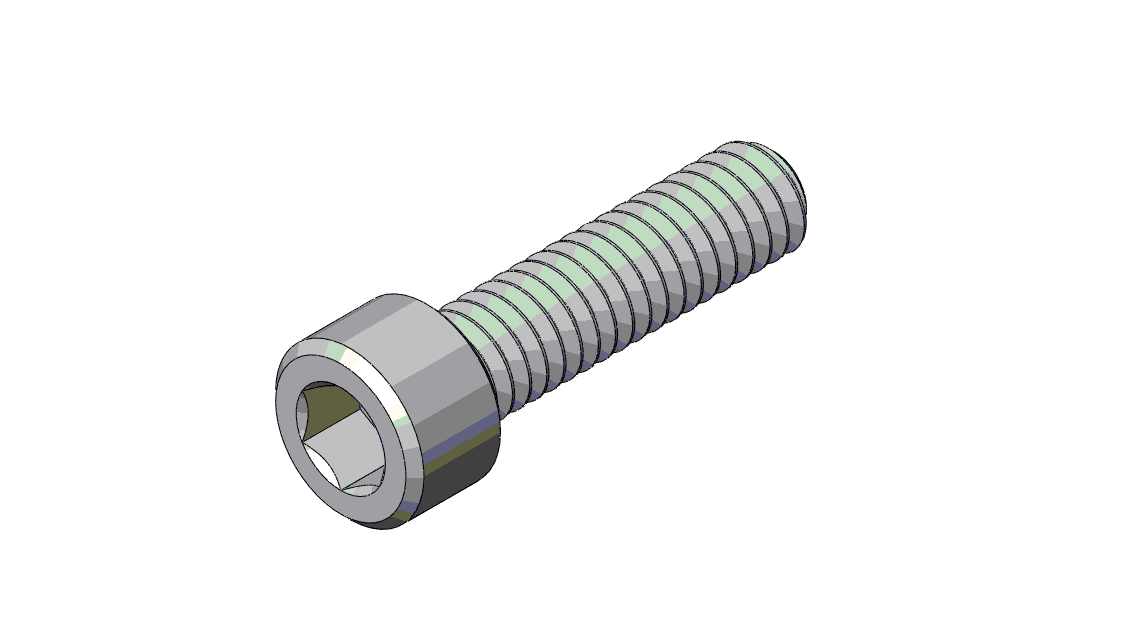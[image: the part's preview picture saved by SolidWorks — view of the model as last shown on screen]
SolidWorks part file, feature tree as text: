
SOLIDWORKS PART (.sldprt)
format: sldprt  version: not decoded by parser v0  size: 1,038,848 bytes
history: native  units: mm
features: sketch x7, chamfer x3, extrude x2, cut_extrude x2, material x1, helix x1, sweep x1 (+15 scaffold rows collapsed)
feature tree (32):
  scaffold x15  (default folders/planes/origin — collapsed)
  material  "Material <not specified>"
  sketch  "Sketch1"  dims[OD=4.1656mm]
  extrude  "Extrude1"  Depth=15.875mm screw length=15.875mm
  sketch  "Sketch2"
  helix  "Helix/Spiral1"  Pitch=16.66875mm pitch=0.79375mm
  chamfer  "Chamfer3"  Distance=0.595313mm Angle=45deg
  sketch  "Sketch3"  dims[c1.D1=~0.099219mm c1.D2=~0.396875mm c1.D3=~1.069256mm c2.D3=60.0deg]
  sweep  "Cut-Sweep1"
  sketch  "Sketch6"  dims[head dia=6.858mm]
  extrude  "Extrude2"  Depth=4.1656mm head depth=4.1656mm
  sketch  "Sketch7"  dims[hex dia=~3.571875mm]
  cut_extrude  "Cut-Extrude1"  Depth=2.678906mm
  sketch  "Sketch8"
  cut_extrude  "Cut-Extrude2"  Depth=0.41656mm
  chamfer  "Chamfer1"  Distance=0.41656mm Angle=45deg
  chamfer  "Chamfer2"  Distance=0.20828mm Angle=45deg
  sketch  "Sketch9"  dims[c1.D1=~4.365625mm c1.D2=4.1656mm c1.D3=6.858mm c1.D4=15.875mm c2.D4=0.635mm c2.D5=0.3302mm]
decode coverage: 13 of 16 modeling features carry decoded parameters
note: ~ marks probable driven/reference dimensions
note: suppression state not decoded; provenance and decode notes live in map.json
